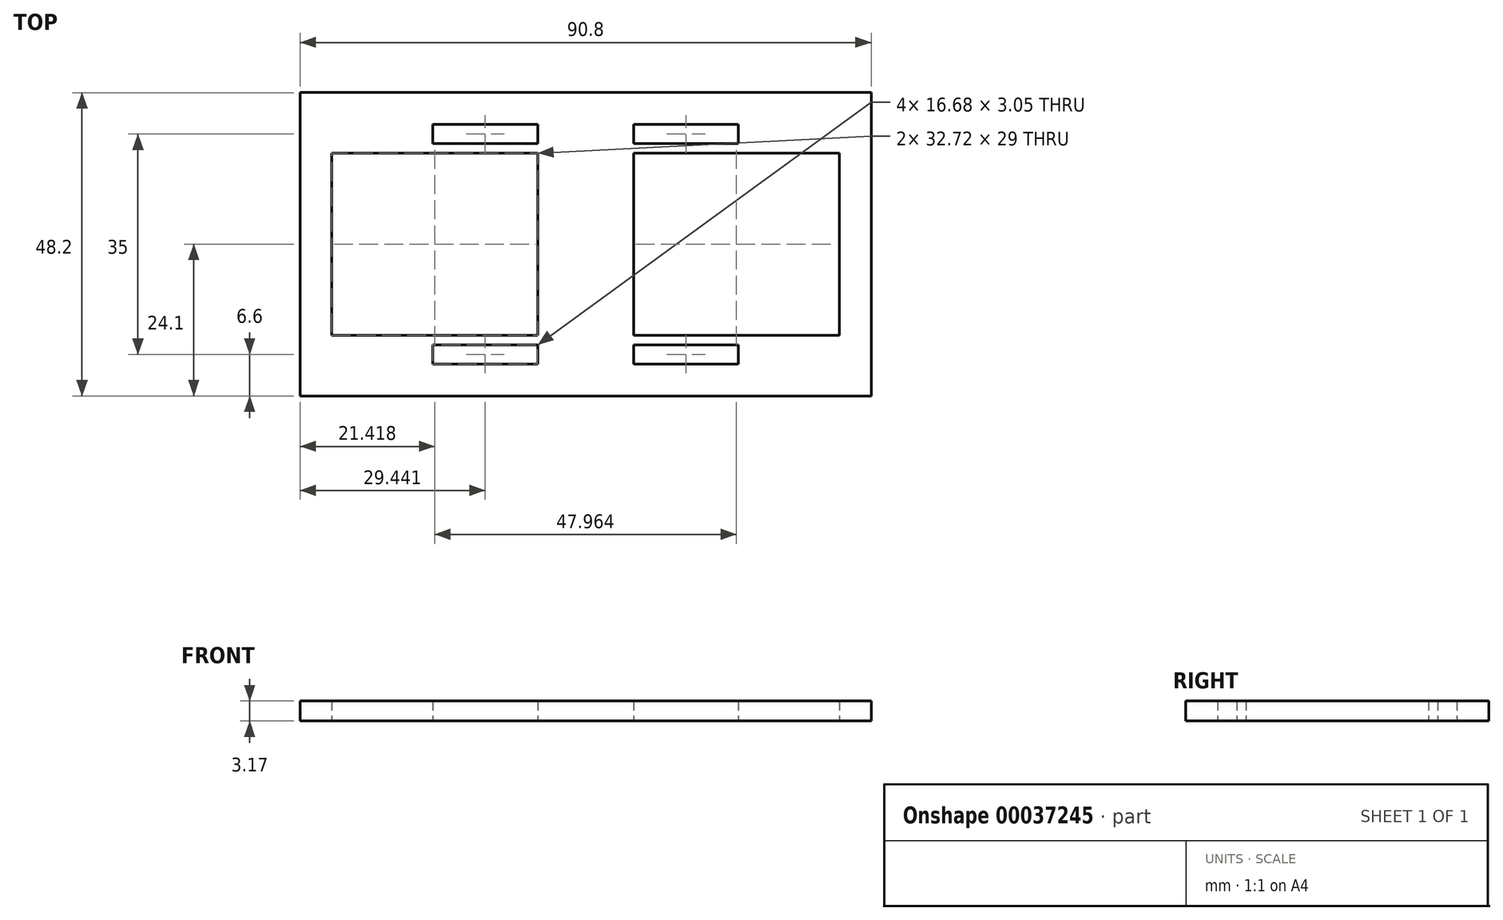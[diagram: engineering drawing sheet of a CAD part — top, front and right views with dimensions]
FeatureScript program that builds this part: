
annotation { "Feature Type Name" : "Feature", "Feature Type Description" : "" }
export const myFeature = defineFeature(function(context is Context, id is Id, definition is map)
    precondition{}
    {
        {
            var Q0;
            Q0=qCreatedBy(makeId("Top.planeOp"),FACE);
            var sketch = newSketch(context, id + "F0", { "sketchPlane" : qUnion([Q0])});
            skLineSegment(sketch, "E0.rect.bottom", {"start": v(45.4, 24.1) * mm, "end": v(-45.4, 24.1) * mm});
            skLineSegment(sketch, "E0.rect.top", {"start": v(45.4, -24.1) * mm, "end": v(-45.4, -24.1) * mm});
            skLineSegment(sketch, "E0.rect.left", {"start": v(45.4, 24.1) * mm, "end": v(45.4, -24.1) * mm});
            skLineSegment(sketch, "E0.rect.right", {"start": v(-45.4, 24.1) * mm, "end": v(-45.4, -24.1) * mm});
            skPoint(sketch, "E0.rect.middle", {"position": v(0, 0) * mm});
            skLineSegment(sketch, "E1.rect.bottom", {"start": v(40.34, 14.5) * mm, "end": v(7.62, 14.5) * mm});
            skLineSegment(sketch, "E1.rect.top", {"start": v(40.34, -14.5) * mm, "end": v(7.62, -14.5) * mm});
            skLineSegment(sketch, "E1.rect.left", {"start": v(40.34, 14.5) * mm, "end": v(40.34, -14.5) * mm});
            skLineSegment(sketch, "E1.rect.right", {"start": v(7.62, 14.5) * mm, "end": v(7.62, -14.5) * mm});
            skPoint(sketch, "E1.rect.middle", {"position": v(23.98, 0) * mm});
            skLineSegment(sketch, "E2.rect.bottom", {"start": v(-40.34, 14.5) * mm, "end": v(-7.62, 14.5) * mm});
            skLineSegment(sketch, "E2.rect.top", {"start": v(-40.34, -14.5) * mm, "end": v(-7.62, -14.5) * mm});
            skLineSegment(sketch, "E2.rect.left", {"start": v(-40.34, 14.5) * mm, "end": v(-40.34, -14.5) * mm});
            skLineSegment(sketch, "E2.rect.right", {"start": v(-7.62, 14.5) * mm, "end": v(-7.62, -14.5) * mm});
            skPoint(sketch, "E2.rect.middle", {"position": v(-23.98, 0) * mm});
            skLineSegment(sketch, "E3", {"start": v(-23.98, 0) * mm, "end": v(23.98, 0) * mm, "construction": true});
            skLineSegment(sketch, "E4.rect.bottom", {"start": v(-24.3, 19.02) * mm, "end": v(24.3, 19.02) * mm, "construction": true});
            skLineSegment(sketch, "E4.rect.top", {"start": v(-24.3, 15.98) * mm, "end": v(24.3, 15.98) * mm, "construction": true});
            skLineSegment(sketch, "E4.rect.left", {"start": v(-24.3, 19.02) * mm, "end": v(-24.3, 15.98) * mm, "construction": true});
            skLineSegment(sketch, "E4.rect.right", {"start": v(24.3, 19.02) * mm, "end": v(24.3, 15.98) * mm, "construction": true});
            skPoint(sketch, "E4.rect.middle", {"position": v(0, 17.5) * mm});
            skLineSegment(sketch, "E5.rect.bottom", {"start": v(24.3, -19.02) * mm, "end": v(-24.3, -19.02) * mm, "construction": true});
            skLineSegment(sketch, "E5.rect.top", {"start": v(24.3, -15.98) * mm, "end": v(-24.3, -15.98) * mm, "construction": true});
            skLineSegment(sketch, "E5.rect.left", {"start": v(24.3, -19.02) * mm, "end": v(24.3, -15.98) * mm, "construction": true});
            skLineSegment(sketch, "E5.rect.right", {"start": v(-24.3, -19.02) * mm, "end": v(-24.3, -15.98) * mm, "construction": true});
            skPoint(sketch, "E5.rect.middle", {"position": v(0, -17.5) * mm});
            skLineSegment(sketch, "E6.bottom", {"start": v(-24.3, 19.02) * mm, "end": v(-7.62, 19.02) * mm});
            skLineSegment(sketch, "E6.top", {"start": v(-24.3, 15.98) * mm, "end": v(-7.62, 15.98) * mm});
            skLineSegment(sketch, "E6.left", {"start": v(-24.3, 19.02) * mm, "end": v(-24.3, 15.98) * mm});
            skLineSegment(sketch, "E6.right", {"start": v(-7.62, 19.02) * mm, "end": v(-7.62, 15.98) * mm});
            skLineSegment(sketch, "E7.bottom", {"start": v(7.62, 19.02) * mm, "end": v(24.3, 19.02) * mm});
            skLineSegment(sketch, "E7.top", {"start": v(7.62, 15.98) * mm, "end": v(24.3, 15.98) * mm});
            skLineSegment(sketch, "E7.left", {"start": v(7.62, 19.02) * mm, "end": v(7.62, 15.98) * mm});
            skLineSegment(sketch, "E7.right", {"start": v(24.3, 19.02) * mm, "end": v(24.3, 15.98) * mm});
            skLineSegment(sketch, "E8.bottom", {"start": v(24.3, -19.02) * mm, "end": v(7.62, -19.02) * mm});
            skLineSegment(sketch, "E8.top", {"start": v(24.3, -15.98) * mm, "end": v(7.62, -15.98) * mm});
            skLineSegment(sketch, "E8.left", {"start": v(24.3, -19.02) * mm, "end": v(24.3, -15.98) * mm});
            skLineSegment(sketch, "E8.right", {"start": v(7.62, -19.02) * mm, "end": v(7.62, -15.98) * mm});
            skLineSegment(sketch, "E9.bottom", {"start": v(-24.3, -15.98) * mm, "end": v(-7.62, -15.98) * mm});
            skLineSegment(sketch, "E9.top", {"start": v(-24.3, -19.02) * mm, "end": v(-7.62, -19.02) * mm});
            skLineSegment(sketch, "E9.left", {"start": v(-24.3, -15.98) * mm, "end": v(-24.3, -19.02) * mm});
            skLineSegment(sketch, "E9.right", {"start": v(-7.62, -15.98) * mm, "end": v(-7.62, -19.02) * mm});
            skSolve(sketch);
        }
        {
            var Q0;
            Q0=makeQuery(id+"F0.imprint","IMPRINT",FACE,{"disambiguationData":[TD([[makeQuery(id+"F0.imprint","IMPRINT",EDGE,{"derivedFrom":sQuery(id+"F0.wireOp",EDGE,"E0.rect.bottom")}),1.0]])]});
            extrude(context, id + "F1", {"entities" : qUnion([Q0]), "depth" : 3.17 * mm});
        }
    });
